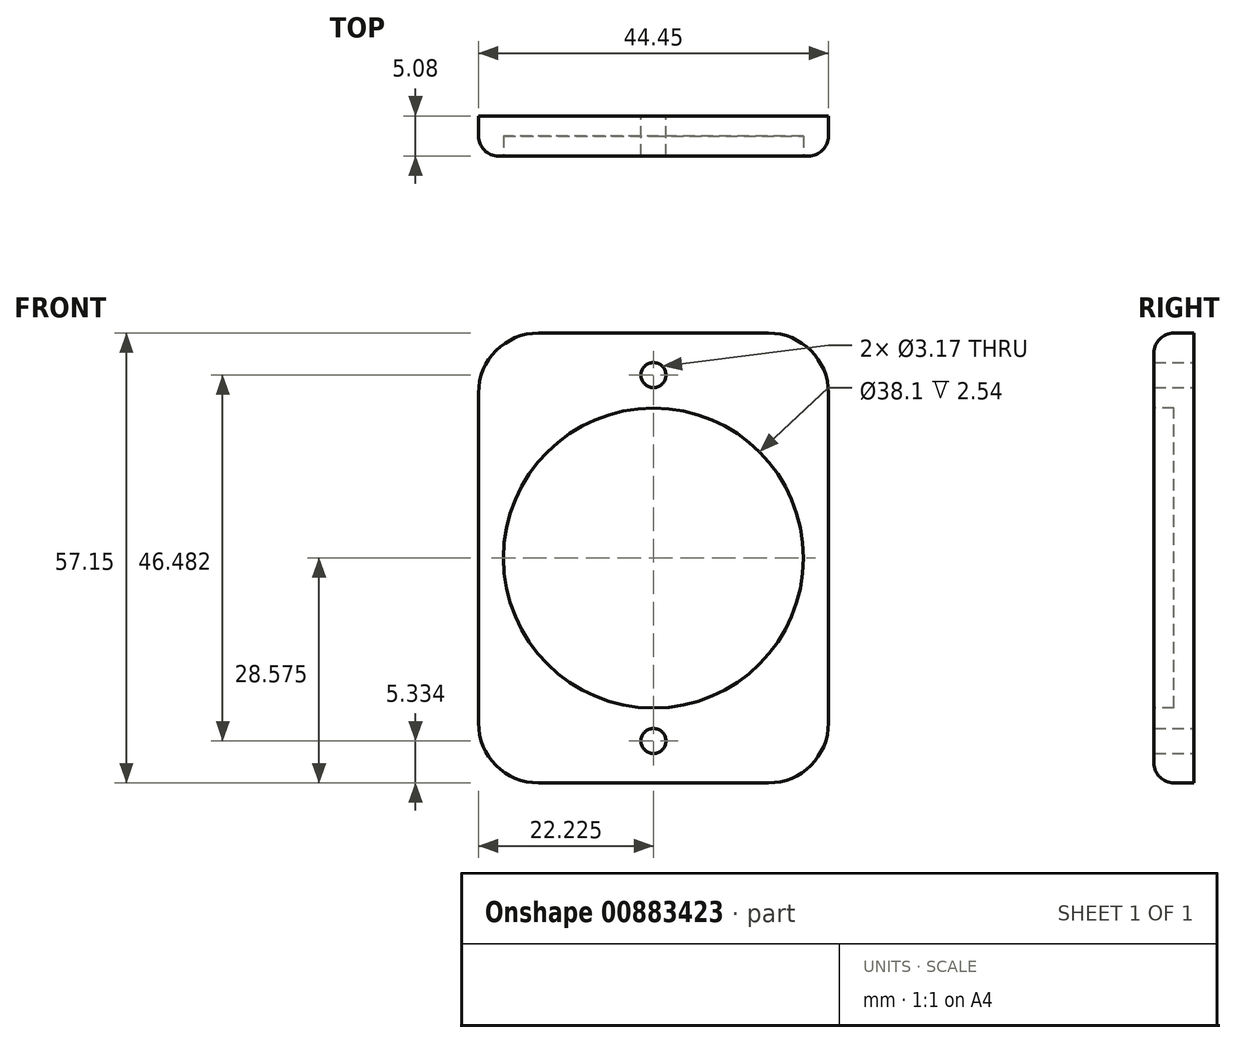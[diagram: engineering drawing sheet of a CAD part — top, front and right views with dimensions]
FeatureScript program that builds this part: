
annotation { "Feature Type Name" : "Feature", "Feature Type Description" : "" }
export const myFeature = defineFeature(function(context is Context, id is Id, definition is map)
    precondition{}
    {
        {
            var Q0;
            Q0=qCreatedBy(makeId("Front.planeOp"),FACE);
            var sketch = newSketch(context, id + "F0", { "sketchPlane" : qUnion([Q0])});
            skLineSegment(sketch, "E0.bottom", {"start": v(7.62, 0) * mm, "end": v(36.83, 0) * mm});
            skLineSegment(sketch, "E0.top", {"start": v(7.62, 57.15) * mm, "end": v(36.83, 57.15) * mm});
            skLineSegment(sketch, "E0.left", {"start": v(0, 7.62) * mm, "end": v(0, 49.53) * mm});
            skLineSegment(sketch, "E0.right", {"start": v(44.45, 7.62) * mm, "end": v(44.45, 49.53) * mm});
            skPoint(sketch, "E1.visualSharp", {"position": v(0, 57.15) * mm});
            skArc(sketch, "E1.filletArc", {"start": v(7.62, 57.15) * mm, "mid": v(2.23, 54.92) * mm, "end": v(0, 49.53) * mm});
            skPoint(sketch, "E2.visualSharp", {"position": v(44.45, 57.15) * mm});
            skArc(sketch, "E2.filletArc", {"start": v(44.45, 49.53) * mm, "mid": v(42.22, 54.92) * mm, "end": v(36.83, 57.15) * mm});
            skPoint(sketch, "E3.visualSharp", {"position": v(0, 0) * mm});
            skArc(sketch, "E3.filletArc", {"start": v(0, 7.62) * mm, "mid": v(2.23, 2.23) * mm, "end": v(7.62, 0) * mm});
            skPoint(sketch, "E4.visualSharp", {"position": v(44.45, 0) * mm});
            skArc(sketch, "E4.filletArc", {"start": v(36.83, 0) * mm, "mid": v(42.22, 2.23) * mm, "end": v(44.45, 7.62) * mm});
            skSolve(sketch);
        }
        {
            var Q0;
            Q0 = qSketchRegion(id + "F0", true);
            extrude(context, id + "F1", {"entities" : qUnion([Q0]), "depth" : 5.08 * mm, "offsetDistance" : 25.4 * mm});
        }
        {
            var Q0;
            Q0=qCreatedBy(makeId("Front.planeOp"),FACE);
            var sketch = newSketch(context, id + "F2", { "sketchPlane" : qUnion([Q0])});
            skLineSegment(sketch, "E5", {"start": v(22.22, 66.4) * mm, "end": v(22.22, -3.5) * mm, "construction": true});
            skLineSegment(sketch, "E6", {"start": v(-3.16, 28.57) * mm, "end": v(41.5, 28.57) * mm, "construction": true});
            skCircle(sketch, "E7", {"center": v(22.22, 51.82) * mm, "radius": 1.59 * mm});
            skCircle(sketch, "E8", {"center": v(22.22, 5.33) * mm, "radius": 1.59 * mm});
            skSolve(sketch);
        }
        {
            var Q0;
            Q0 = qSketchRegion(id + "F2", true);
            extrude(context, id + "F3", {"entities" : qUnion([Q0]), "operationType" : NewBodyOperationType.REMOVE, "depth" : 25.4 * mm, "offsetDistance" : 25.4 * mm});
        }
        {
            var Q0;
            Q0=makeQuery(id+"F1.opExtrude","CAP_EDGE",EDGE,{"disambiguationData":[OSD([sQuery(id+"F0.wireOp",EDGE,"E0.top")])],"isStart":false});
            fillet(context, id + "F4", {"entities" : qUnion([Q0]), "radius" : 2.54 * mm, "tangentPropagation" : true, "allowEdgeOverflow" : false});
        }
        {
            var Q0;
            Q0=makeQuery(id+"F1.opExtrude","CAP_FACE",FACE,{"disambiguationData":[OSD([sQuery(id+"F0.wireOp",EDGE,"E0.bottom"),sQuery(id+"F0.wireOp",EDGE,"E0.top"),sQuery(id+"F0.wireOp",EDGE,"E0.left"),sQuery(id+"F0.wireOp",EDGE,"E0.right"),sQuery(id+"F0.wireOp",EDGE,"E1.filletArc"),sQuery(id+"F0.wireOp",EDGE,"E2.filletArc"),sQuery(id+"F0.wireOp",EDGE,"E3.filletArc"),sQuery(id+"F0.wireOp",EDGE,"E4.filletArc")])],"isStart":false});
            var sketch = newSketch(context, id + "F5", { "sketchPlane" : qUnion([Q0])});
            skLineSegment(sketch, "E9", {"start": v(22.22, 80.37) * mm, "end": v(22.22, -4.07) * mm, "construction": true});
            skLineSegment(sketch, "E10", {"start": v(-4.01, 28.57) * mm, "end": v(49.43, 28.57) * mm, "construction": true});
            skCircle(sketch, "E11", {"center": v(22.22, 28.57) * mm, "radius": 19.05 * mm});
            skSolve(sketch);
        }
        {
            var Q0;
            Q0 = qSketchRegion(id + "F5", true);
            extrude(context, id + "F6", {"entities" : qUnion([Q0]), "operationType" : NewBodyOperationType.REMOVE, "oppositeDirection" : true, "depth" : 2.54 * mm, "offsetDistance" : 25.4 * mm});
        }
    });
